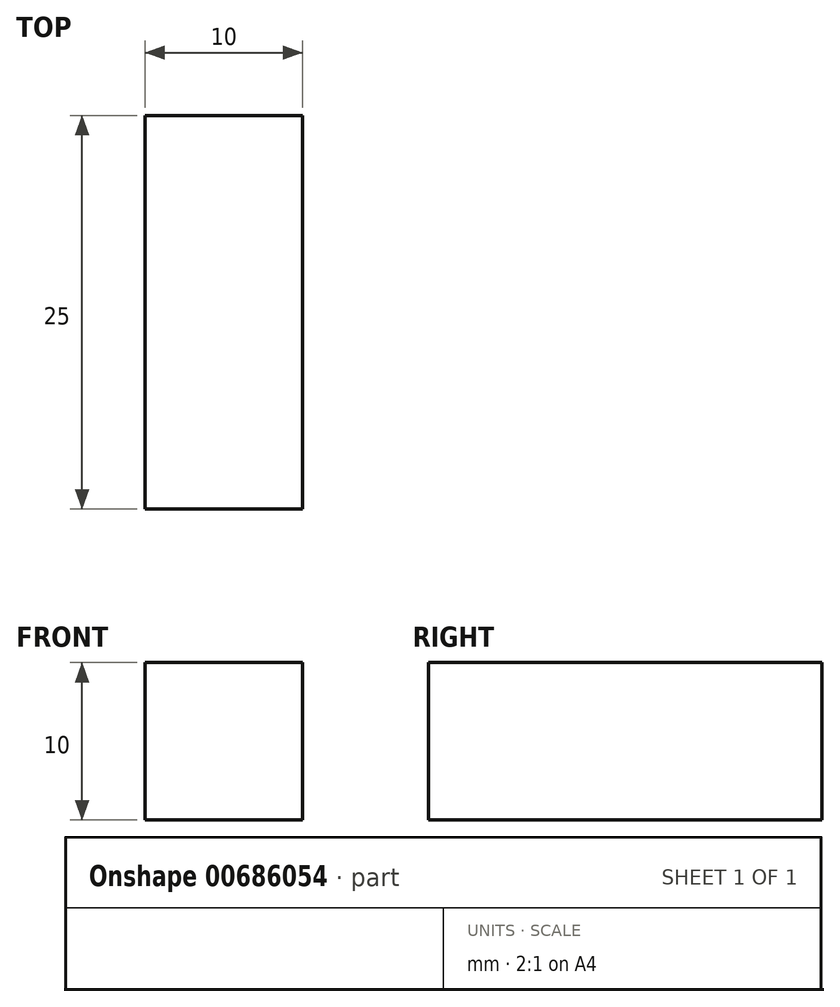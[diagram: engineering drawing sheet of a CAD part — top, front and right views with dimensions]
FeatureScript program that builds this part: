
annotation { "Feature Type Name" : "Feature", "Feature Type Description" : "" }
export const myFeature = defineFeature(function(context is Context, id is Id, definition is map)
    precondition{}
    {
        {
            var Q0;
            Q0=qCreatedBy(makeId("Front.planeOp"),FACE);
            var sketch = newSketch(context, id + "F0", { "sketchPlane" : qUnion([Q0])});
            skLineSegment(sketch, "E0.bottom", {"start": v(-34.15, 26.45) * mm, "end": v(-24.15, 26.45) * mm});
            skLineSegment(sketch, "E0.top", {"start": v(-34.15, 16.45) * mm, "end": v(-24.15, 16.45) * mm});
            skLineSegment(sketch, "E0.left", {"start": v(-34.15, 26.45) * mm, "end": v(-34.15, 16.45) * mm});
            skLineSegment(sketch, "E0.right", {"start": v(-24.15, 26.45) * mm, "end": v(-24.15, 16.45) * mm});
            skSolve(sketch);
        }
        {
            var Q0;
            Q0 = qSketchRegion(id + "F0", true);
            extrude(context, id + "F1", {"entities" : qUnion([Q0]), "depth" : 25 * mm, "offsetDistance" : 25 * mm});
        }
    });
